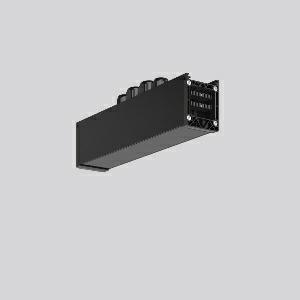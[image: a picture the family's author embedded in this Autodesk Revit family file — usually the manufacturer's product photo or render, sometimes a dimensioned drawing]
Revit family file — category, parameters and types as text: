
# Revit family: linedo_mitteleinspeisung_14pol_b_b_982698_003_1_1f9e
name_source: partatom
category: Lighting Fixtures
units: mm (PartAtom-declared; Revit-internal decimal feet)

## family parameters
Cut with Voids When Loaded = No
Host = Face
Light Source = No
Part Type = Normal
Room Calculation Point = No
Round Connector Dimension = Use Diameter
Shared = No

## types (1)
- LINEDO_Mitteleinspeisung_14pol_B_B
    Apparent Load = 0 VA
    Default Elevation = 1800 mm
    Description = Series: LINEDO
Middle power feed, 14-pole, connection socket / socket. Housing: extruded aluminium profile, powder-coated. Cover made of plastic, surface like housing. LINEDO plug system, plastic, black. 4 cable glands (2 x M20 and 2 x M25). Cable glands on top. Easy connection for rigid or flexible wires.
Colour: black
Length: 312 mm
Width: 58 mm
Height: 76 mm
Weight: 850 g
    Height = 76 mm
    Lamp = 0 x
    Length = 312 mm
    Luminous efficacy = 0 lm/W
    Manufacturer = RZB
    ModVariant = No
    Model = 982698.003.1
    Mounting Place = Ceiling
    Mounting Type = Surface mounted, Pendant
    Number of Poles = 1
    OnlyDefault = Yes
    Power Factor = 1
    Product Name = LINEDO_Mitteleinspeisung_14pol_B_B
    Product group = Surface mounted continuous line luminaire system
    ProductGroupID = 310
    Protection Class = Protection class I
    Protection Degree = IP 54
    RLX_Detail_Level = 1
    RLX_Emergency_Light_Flux = 0 lm
    RLX_Emergency_Type = 0
    RLX_Emergency_Type_DB = No
    RlxData = <blob elided: 23509 chars, md5=f60bc787>
    Standby Power = 0 W
    System Light Flux = 0 lm
    System Power = 0 W
    Type Comments = Product without accessories
    Type Image = 982698.003.1.jpg
    URL = http://relux.com
    VarID = ---
    Voltage = 0 V
    Weight = 0.00 kg
    Width = 58 mm

## geometry (parser evidence)
native form markers: Blend x4, Sweep x11
no freeform markers — native parametric forms only
